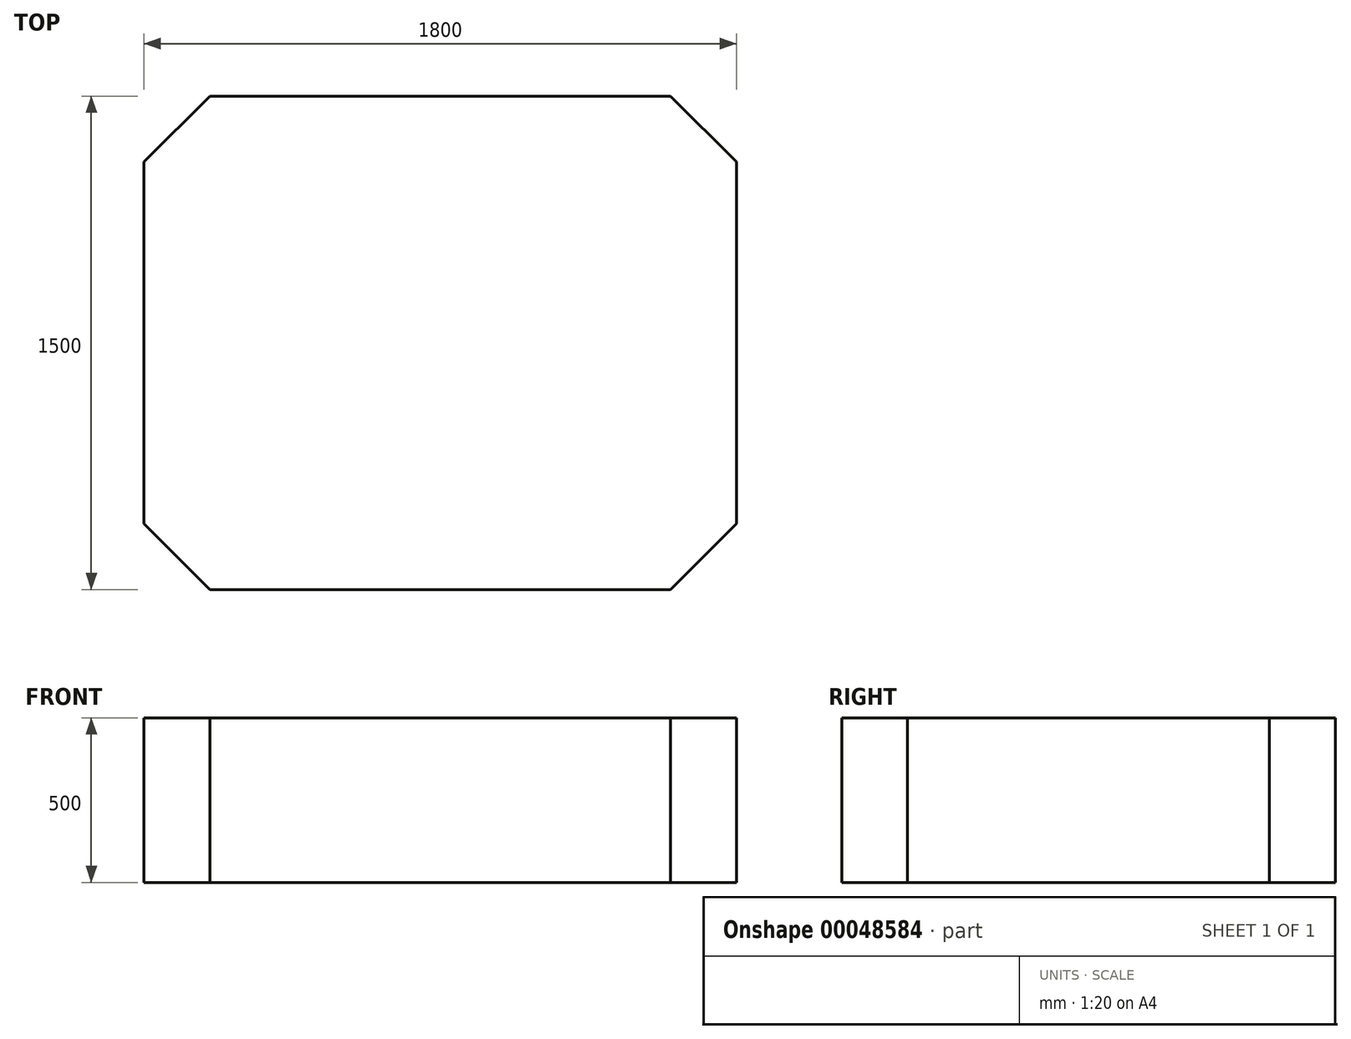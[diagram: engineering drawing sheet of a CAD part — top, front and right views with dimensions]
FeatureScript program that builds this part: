
annotation { "Feature Type Name" : "Feature", "Feature Type Description" : "" }
export const myFeature = defineFeature(function(context is Context, id is Id, definition is map)
    precondition{}
    {
        {
            var Q0;
            Q0=qCreatedBy(makeId("Top.planeOp"),FACE);
            var sketch = newSketch(context, id + "F0", { "sketchPlane" : qUnion([Q0])});
            skLineSegment(sketch, "E0.bottom", {"start": v(-925.1, 775.1) * mm, "end": v(874.9, 775.1) * mm});
            skLineSegment(sketch, "E0.top", {"start": v(-925.1, -724.9) * mm, "end": v(874.9, -724.9) * mm});
            skLineSegment(sketch, "E0.left", {"start": v(-925.1, 775.1) * mm, "end": v(-925.1, -724.9) * mm});
            skLineSegment(sketch, "E0.right", {"start": v(874.9, 775.1) * mm, "end": v(874.9, -724.9) * mm});
            skSolve(sketch);
        }
        {
            var Q0;
            Q0=makeQuery(id+"F0.imprint","IMPRINT",FACE,{"disambiguationData":[TD([[makeQuery(id+"F0.imprint","IMPRINT",EDGE,{"derivedFrom":sQuery(id+"F0.wireOp",EDGE,"E0.bottom")}),-1.0]])]});
            extrude(context, id + "F1", {"entities" : qUnion([Q0]), "depth" : 500 * mm});
        }
        {
            var Q0;
            Q0=makeQuery(id+"F1.opExtrude","SWEPT_EDGE",EDGE,{"disambiguationData":[OSD([sQuery(id+"F0.wireOp",EDGE,"E0.bottom"),sQuery(id+"F0.wireOp",EDGE,"E0.left")])]});
            var Q1;
            Q1=makeQuery(id+"F1.opExtrude","SWEPT_EDGE",EDGE,{"disambiguationData":[OSD([sQuery(id+"F0.wireOp",EDGE,"E0.top"),sQuery(id+"F0.wireOp",EDGE,"E0.left")])]});
            var Q2;
            Q2=makeQuery(id+"F1.opExtrude","SWEPT_EDGE",EDGE,{"disambiguationData":[OSD([sQuery(id+"F0.wireOp",EDGE,"E0.top"),sQuery(id+"F0.wireOp",EDGE,"E0.right")])]});
            var Q3;
            Q3=makeQuery(id+"F1.opExtrude","SWEPT_EDGE",EDGE,{"disambiguationData":[OSD([sQuery(id+"F0.wireOp",EDGE,"E0.bottom"),sQuery(id+"F0.wireOp",EDGE,"E0.right")])]});
            chamfer(context, id + "F2", {"entities" : qUnion([Q0, Q1, Q2, Q3]), "width" : 200 * mm, "tangentPropagation" : true});
        }
    });
